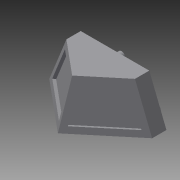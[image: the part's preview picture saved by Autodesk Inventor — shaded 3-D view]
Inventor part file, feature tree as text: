
AUTODESK INVENTOR PART (.ipt)
format: ipt  version: 2015 (Build 190159000, 159)  size: 151,552 bytes
history: native  units: in
note: dims shown in document units (in); Inventor stores cm internally (conversion verified against a paired STEP export)
features: sketch x5, extrude x3, plane x1, loft x1, shell x1, chamfer x1
ambient origin geometry x8: Origin, YZ Plane, XZ Plane, XY Plane, X Axis, Y Axis, Z Axis, Center Point
bodies: Body1 (feature_tree)
feature tree (12):
  sketch  "Sketch1"  dims[d0=0.25in d1=0.25in d2=1.8in]
  plane  "Work Plane2"
  loft  "Loft1"
  shell  "Shell1"  Thickness=1.8in
  extrude  "Extrusion2"  Depth=0.9in
  extrude  "Extrusion3"  Depth=0.25in
  extrude  "Extrusion4"  Depth=0.6in
  chamfer  "Chamfer1"  Distance=1.2in
  sketch  "Sketch2"  dims[d3=0.9in d4=0.9in]
  sketch  "Sketch4"  dims[d5=1.0in d8=0.25in]
  sketch  "Sketch5"  dims[d9=0.25in d10=0.6in]
  sketch  "Sketch6"  dims[d11=0.6in d12=1.2in d15=0.0in d16=0.0in d17=90.0deg d18=0.0in d19=90.0deg d20=0.1in d21=0.1in d22=0.1in d23=0.1in d24=0.1in d25=0.05in d26=0.0in d27=0.1in d29=0.1in d32=0.1in d34=0.1in d35=0.05in d36=0.0in d37=0.275in d38=0.275in d39=0.125in d40=0.125in d41=0.125in d42=0.9in d43=0.125in d44=0.125in d45=0.125in d46=0.125in d47=0.0in d48=0.01in d49=0.125in d50=45.0deg]
